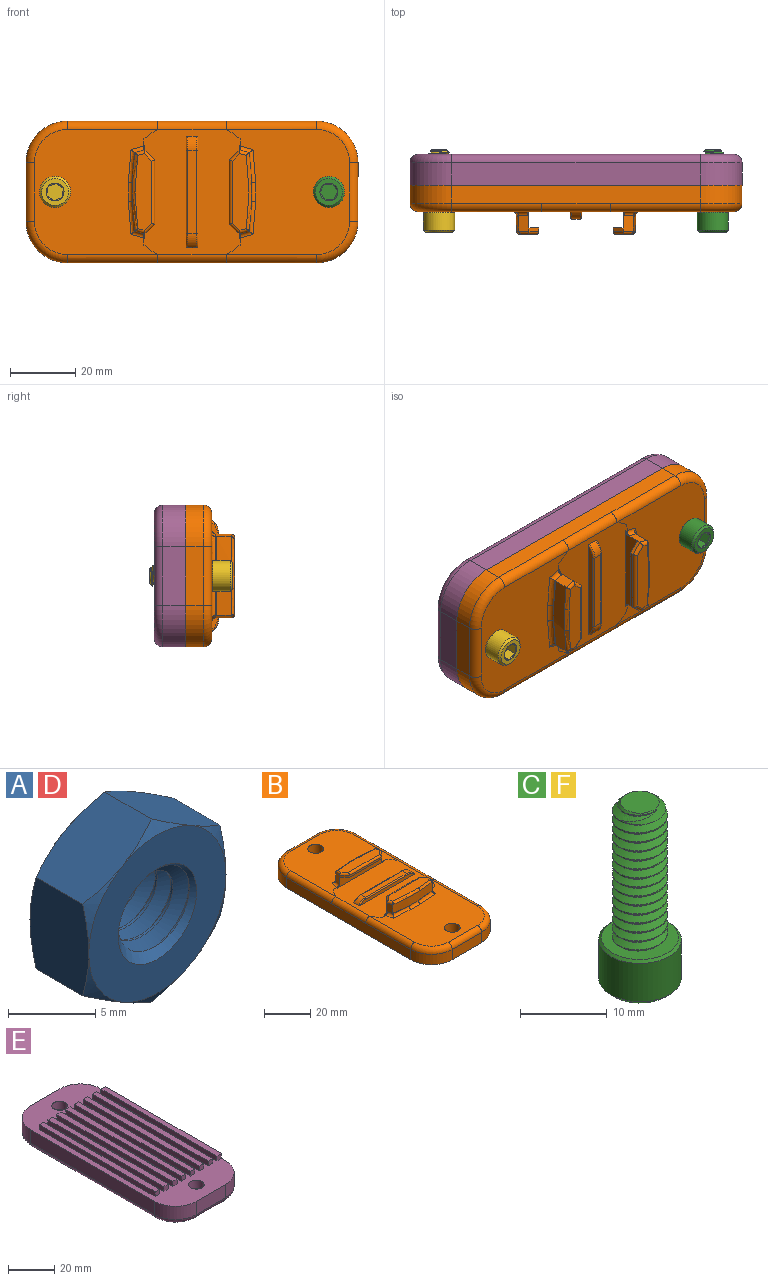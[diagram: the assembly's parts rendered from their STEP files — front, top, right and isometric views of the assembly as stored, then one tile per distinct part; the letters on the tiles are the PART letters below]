
ASSEMBLY  parts=6 mates=13
PART A: 26 faces, bbox 13.4x6.2x13.4 mm
  f0: bspline ~6.35x6.35mm, area 51.9mm2, adj f1,f11,f12,f19
  f1: cylinder r=2.35mm len=4.7mm, axis (0,-1,0), area 5.7mm2, adj f0,f2,f12,f19
  f2: bspline ~6.35x6.35mm, area 51.8mm2, adj f1,f11,f12,f19
  f3: plane 11.11x11.11mm, normal (0,1,0), area 65.3mm2, adj f11,f12,f13,f14,f15,f16,f17,f18
  f4: plane 6.08x5.3mm, normal (-0.5,0,-0.87), area 28.4mm2, adj f5,f9,f13,f18,f23,f24
  f5: plane 6.95x5.3mm, normal (-1,0,0), area 28.4mm2, adj f4,f6,f17,f18,f24,f25
  f6: plane 6.08x5.3mm, normal (-0.5,0,0.87), area 28.4mm2, adj f5,f7,f16,f17,f20,f25
  f7: plane 6.08x5.3mm, normal (0.5,0,0.87), area 28.4mm2, adj f6,f8,f15,f16,f20,f21
  f8: plane 6.95x5.3mm, normal (1,0,0), area 28.4mm2, adj f7,f9,f14,f15,f21,f22
  f9: plane 6.08x5.3mm, normal (0.5,0,-0.87), area 28.4mm2, adj f4,f8,f13,f14,f22,f23
  f10: plane 11.11x11.11mm, normal (0,-1,0), area 65.3mm2, adj f11,f19,f20,f21,f22,f23,f24,f25
  f11: cylinder r=3.17mm len=6.35mm, axis (0,-1,0), area 11.9mm2, adj f0,f2,f3,f10
  f12: cone r=3.17mm half-angle=45deg, axis (0,1,0), area 10.5mm2, adj f0,f1,f2,f3
  f13: cone r=5.56mm half-angle=60deg, axis (0,-1,0), area 3mm2, adj f3,f4,f9
  f14: cone r=5.56mm half-angle=60deg, axis (0,-1,0), area 3mm2, adj f3,f8,f9
  f15: cone r=5.56mm half-angle=60deg, axis (0,-1,0), area 3mm2, adj f3,f7,f8
  f16: cone r=5.56mm half-angle=60deg, axis (0,-1,0), area 3mm2, adj f3,f6,f7
  f17: cone r=5.56mm half-angle=60deg, axis (0,-1,0), area 3mm2, adj f3,f5,f6
  f18: cone r=5.56mm half-angle=60deg, axis (0,-1,0), area 3mm2, adj f3,f4,f5
  f19: cone r=3.17mm half-angle=45deg, axis (0,-1,0), area 10.5mm2, adj f0,f1,f2,f10
  f20: cone r=5.56mm half-angle=60deg, axis (0,1,0), area 3mm2, adj f6,f7,f10
  f21: cone r=5.56mm half-angle=60deg, axis (0,1,0), area 3mm2, adj f7,f8,f10
  f22: cone r=5.56mm half-angle=60deg, axis (0,1,0), area 3mm2, adj f8,f9,f10
  f23: cone r=5.56mm half-angle=60deg, axis (0,1,0), area 3mm2, adj f4,f9,f10
  f24: cone r=5.56mm half-angle=60deg, axis (0,1,0), area 3mm2, adj f4,f5,f10
  f25: cone r=5.56mm half-angle=60deg, axis (0,1,0), area 3mm2, adj f5,f6,f10
PART B: 124 faces, bbox 45.6x103.9x15.2 mm
  f0: bspline ~18.94x3.73mm, area 1mm2, adj f32,f44,f118,f119
  f1: bspline ~21.05x3.89mm, area 1mm2, adj f33,f49,f111,f112
  f2: plane 2.71x2.54mm, normal (0,-1,0), area 6.9mm2, adj f25,f27,f94,f108
  f3: plane 2.71x2.54mm, normal (0,1,0), area 6.9mm2, adj f25,f27,f94,f108
  f4: plane 71.12x2.71mm, normal (0,0,-1), area 192.8mm2, adj f5,f6,f106,f109
  f5: plane 2.71x2.54mm, normal (0,-1,0), area 6.9mm2, adj f4,f27,f106,f109
  f6: plane 2.71x2.54mm, normal (0,1,0), area 6.9mm2, adj f4,f27,f106,f109
  f7: plane 71.12x2.71mm, normal (0,0,-1), area 192.8mm2, adj f8,f9,f104,f107
  f8: plane 2.71x2.54mm, normal (0,-1,0), area 6.9mm2, adj f7,f27,f104,f107
  f9: plane 2.71x2.54mm, normal (0,1,0), area 6.9mm2, adj f7,f27,f104,f107
  f10: plane 71.12x2.71mm, normal (0,0,-1), area 192.8mm2, adj f11,f12,f102,f105
  f11: plane 2.71x2.54mm, normal (0,-1,0), area 6.9mm2, adj f10,f27,f102,f105
  f12: plane 2.71x2.54mm, normal (0,1,0), area 6.9mm2, adj f10,f27,f102,f105
  f13: plane 71.12x2.71mm, normal (0,0,-1), area 192.8mm2, adj f14,f15,f100,f103
  f14: plane 2.71x2.54mm, normal (0,-1,0), area 6.9mm2, adj f13,f27,f100,f103
  f15: plane 2.71x2.54mm, normal (0,1,0), area 6.9mm2, adj f13,f27,f100,f103
  f16: plane 71.12x2.71mm, normal (0,0,-1), area 192.8mm2, adj f17,f18,f98,f101
  f17: plane 2.71x2.54mm, normal (0,-1,0), area 6.9mm2, adj f16,f27,f98,f101
  f18: plane 2.71x2.54mm, normal (0,1,0), area 6.9mm2, adj f16,f27,f98,f101
  f19: plane 71.12x2.71mm, normal (0,0,-1), area 192.8mm2, adj f20,f21,f96,f99
  f20: plane 2.71x2.54mm, normal (0,-1,0), area 6.9mm2, adj f19,f27,f96,f99
  f21: plane 2.71x2.54mm, normal (0,1,0), area 6.9mm2, adj f19,f27,f96,f99
  f22: plane 71.12x2.71mm, normal (0,0,-1), area 192.8mm2, adj f23,f24,f95,f97
  f23: plane 2.71x2.54mm, normal (0,-1,0), area 6.9mm2, adj f22,f27,f95,f97
  f24: plane 2.71x2.54mm, normal (0,1,0), area 6.9mm2, adj f22,f27,f95,f97
  f25: plane 76.2x5.46mm, normal (1,0,0), area 235.5mm2, adj f2,f3,f27,f79,f80,f82,f83,f85
  f26: plane 17.98x5.46mm, normal (0,-1,0), area 98.2mm2, adj f27,f80,f81,f86
  f27: plane 101.6x43.38mm, normal (0,0,-1), area 2654.9mm2, adj f2,f3,f5,f6,f8,f9,f11,f12
  f28: plane 38.42x37.89mm, normal (0,0,1), area 1093.7mm2, adj f40,f77,f85,f87,f89,f91,f93,f118
  f29: plane 38.42x37.89mm, normal (0,0,1), area 1093.7mm2, adj f40,f76,f82,f84,f86,f88,f90,f111
  f30: plane 17.98x5.46mm, normal (0,1,0), area 98.2mm2, adj f27,f78,f79,f89
  f31: plane 4.73x3.1mm, normal (-0.97,0.26,0), area 15.2mm2, adj f36,f44,f45,f54,f66,f122,f123
  f32: plane 4.73x3.1mm, normal (0.97,0.26,0), area 15.2mm2, adj f0,f44,f47,f54,f63,f117,f118
  f33: plane 4.73x3.1mm, normal (-0.97,-0.26,0), area 15.2mm2, adj f1,f38,f49,f51,f55,f110,f111
  f34: plane 4.73x3.1mm, normal (0.97,-0.26,0), area 15.2mm2, adj f35,f39,f49,f51,f59,f115,f116
  f35: bspline ~18.94x3.73mm, area 1mm2, adj f34,f49,f114,f116
  f36: bspline ~21.05x3.89mm, area 1mm2, adj f31,f44,f121,f123
  f37: plane 19.82x1mm, normal (0,1,0), area 19.8mm2, adj f38,f39,f52,f58
  f38: plane 3x3mm, normal (-0.71,0.71,0), area 4.2mm2, adj f33,f37,f52,f56
  f39: plane 3x2.83mm, normal (0.73,0.69,0), area 4.1mm2, adj f34,f37,f52,f60
  f40: plane 38.57x30.25mm, normal (0,0,1), area 964.3mm2, adj f28,f29,f41,f42,f51,f54,f67,f68
  f41: plane 32.77x1.75mm, normal (0,-1,0), area 53.6mm2, adj f40,f72,f73,f74
  f42: plane 32.77x1.75mm, normal (0,1,0), area 53.6mm2, adj f40,f69,f70,f71
  f43: plane 25.65x2.65mm, normal (0,0,1), area 68mm2, adj f67,f68,f70,f73
  f44: cylinder r=95.04mm len=23.99mm, axis (0,0,-1), area 111.6mm2, adj f0,f31,f32,f36,f65,f120
  f45: plane 3x3mm, normal (-0.71,-0.71,0), area 4.2mm2, adj f31,f46,f53,f64
  f46: plane 19.82x1mm, normal (0,-1,0), area 19.8mm2, adj f45,f47,f53,f62
  f47: plane 3x2.83mm, normal (0.73,-0.69,0), area 4.1mm2, adj f32,f46,f53,f61
  f48: plane 23.42x4.86mm, normal (0,0,1), area 102.1mm2, adj f61,f62,f63,f64,f65,f66
  f49: cylinder r=95.04mm len=23.99mm, axis (0,0,-1), area 111.6mm2, adj f1,f33,f34,f35,f57,f113
  f50: plane 23.42x4.86mm, normal (0,0,1), area 102.1mm2, adj f55,f56,f57,f58,f59,f60
  f51: plane 28.42x5.14mm, normal (0,1,0), area 129mm2, adj f33,f34,f40,f52,f110,f115
  f52: plane 25.65x3mm, normal (0,0,-1), area 68.2mm2, adj f37,f38,f39,f51
  f53: plane 25.65x3mm, normal (0,0,-1), area 68.2mm2, adj f45,f46,f47,f54
  f54: plane 28.42x5.14mm, normal (0,-1,0), area 129mm2, adj f31,f32,f40,f53,f117,f122
  f55: cylinder r=1mm len=3.36mm, axis (-0.26,0.97,0), area 4.1mm2, adj f33,f50,f56,f57
  f56: cylinder r=1mm len=3.71mm, axis (0.71,0.71,0), area 5.9mm2, adj f38,f50,f55,f58
  f57: torus R=94.04mm, axis (0,0,1), area 36.6mm2, adj f49,f50,f55,f59
  f58: cylinder r=1mm len=19.82mm, axis (1,0,0), area 30.5mm2, adj f37,f50,f56,f60
  f59: cylinder r=1mm len=3.36mm, axis (-0.26,-0.97,0), area 4.1mm2, adj f34,f50,f57,f60
  f60: cylinder r=1mm len=3.69mm, axis (0.69,-0.73,0), area 5.7mm2, adj f39,f50,f58,f59
  f61: cylinder r=1mm len=3.69mm, axis (-0.69,-0.73,0), area 5.7mm2, adj f47,f48,f62,f63
  f62: cylinder r=1mm len=19.82mm, axis (-1,0,0), area 30.5mm2, adj f46,f48,f61,f64
  f63: cylinder r=1mm len=3.36mm, axis (0.26,-0.97,0), area 4.1mm2, adj f32,f48,f61,f65
  f64: cylinder r=1mm len=3.71mm, axis (-0.71,0.71,0), area 5.9mm2, adj f45,f48,f62,f66
  f65: torus R=94.04mm, axis (0,0,1), area 36.6mm2, adj f44,f48,f63,f66
  f66: cylinder r=1mm len=3.36mm, axis (0.26,0.97,0), area 4.1mm2, adj f31,f48,f64,f65
  f67: cylinder r=5mm len=4.18mm, axis (0,-1,0), area 13.1mm2, adj f40,f43,f69,f72
  f68: cylinder r=5mm len=4.18mm, axis (0,-1,0), area 13.1mm2, adj f40,f43,f71,f74
  f69: torus R=4.5mm, axis (0,1,0), area 3.6mm2, adj f40,f42,f67,f70
  f70: cylinder r=0.5mm len=25.65mm, axis (1,0,0), area 20.1mm2, adj f42,f43,f69,f71
  f71: torus R=4.5mm, axis (0,1,0), area 3.6mm2, adj f40,f42,f68,f70
  f72: torus R=4.5mm, axis (0,1,0), area 3.6mm2, adj f40,f41,f67,f73
  f73: cylinder r=0.5mm len=25.65mm, axis (-1,0,0), area 20.1mm2, adj f41,f43,f72,f74
  f74: torus R=4.5mm, axis (0,1,0), area 3.6mm2, adj f40,f41,f68,f73
  f75: plane 76.2x5.46mm, normal (-1,0,0), area 416.1mm2, adj f27,f78,f81,f90,f92,f93
  f76: cylinder r=3.38mm len=8mm, axis (0,0,-1), area 169.8mm2, adj f27,f29
  f77: cylinder r=3.38mm len=8mm, axis (0,0,-1), area 169.8mm2, adj f27,f28
  f78: cylinder r=12.7mm len=12.7mm, axis (0,0,1), area 108.9mm2, adj f27,f30,f75,f91
  f79: cylinder r=12.7mm len=12.7mm, axis (0,0,-1), area 108.9mm2, adj f25,f27,f30,f87
  f80: cylinder r=12.7mm len=12.7mm, axis (0,0,-1), area 108.9mm2, adj f25,f26,f27,f84
  f81: cylinder r=12.7mm len=12.7mm, axis (0,0,1), area 108.9mm2, adj f26,f27,f75,f88
  f82: cylinder r=2.54mm len=27.67mm, axis (0,-1,0), area 110.4mm2, adj f25,f29,f83,f84
  f83: cylinder r=2.54mm len=20.85mm, axis (0,1,0), area 83.2mm2, adj f25,f40,f82,f85
  f84: torus R=10.16mm, axis (0,0,-1), area 73.8mm2, adj f29,f80,f82,f86
  f85: cylinder r=2.54mm len=27.67mm, axis (0,-1,0), area 110.4mm2, adj f25,f28,f83,f87
  f86: cylinder r=2.54mm len=17.98mm, axis (1,0,0), area 71.7mm2, adj f26,f29,f84,f88
  f87: torus R=10.16mm, axis (0,0,-1), area 73.8mm2, adj f28,f79,f85,f89
  f88: torus R=10.16mm, axis (0,0,-1), area 73.8mm2, adj f29,f81,f86,f90
  f89: cylinder r=2.54mm len=17.98mm, axis (-1,0,0), area 71.7mm2, adj f28,f30,f87,f91
  f90: cylinder r=2.54mm len=27.67mm, axis (0,1,0), area 110.4mm2, adj f29,f75,f88,f92
  f91: torus R=10.16mm, axis (0,0,-1), area 73.8mm2, adj f28,f78,f89,f93
  f92: cylinder r=2.54mm len=20.85mm, axis (0,-1,0), area 83.2mm2, adj f40,f75,f90,f93
  f93: cylinder r=2.54mm len=27.67mm, axis (0,1,0), area 110.4mm2, adj f28,f75,f91,f92
  f94: plane 71.12x2.71mm, normal (0,0,-1), area 192.8mm2, adj f2,f3,f25,f108
  f95: plane 71.12x2.54mm, normal (1,0,0), area 180.6mm2, adj f22,f23,f24,f27
  f96: plane 71.12x2.54mm, normal (1,0,0), area 180.6mm2, adj f19,f20,f21,f27
  f97: plane 71.12x2.54mm, normal (-1,0,0), area 180.6mm2, adj f22,f23,f24,f27
  f98: plane 71.12x2.54mm, normal (1,0,0), area 180.6mm2, adj f16,f17,f18,f27
  f99: plane 71.12x2.54mm, normal (-1,0,0), area 180.6mm2, adj f19,f20,f21,f27
  f100: plane 71.12x2.54mm, normal (1,0,0), area 180.6mm2, adj f13,f14,f15,f27
  f101: plane 71.12x2.54mm, normal (-1,0,0), area 180.6mm2, adj f16,f17,f18,f27
  f102: plane 71.12x2.54mm, normal (1,0,0), area 180.6mm2, adj f10,f11,f12,f27
  f103: plane 71.12x2.54mm, normal (-1,0,0), area 180.6mm2, adj f13,f14,f15,f27
  f104: plane 71.12x2.54mm, normal (1,0,0), area 180.6mm2, adj f7,f8,f9,f27
  f105: plane 71.12x2.54mm, normal (-1,0,0), area 180.6mm2, adj f10,f11,f12,f27
  f106: plane 71.12x2.54mm, normal (1,0,0), area 180.6mm2, adj f4,f5,f6,f27
  f107: plane 71.12x2.54mm, normal (-1,0,0), area 180.6mm2, adj f7,f8,f9,f27
  f108: plane 71.12x2.54mm, normal (1,0,0), area 180.6mm2, adj f2,f3,f27,f94
  f109: plane 71.12x2.54mm, normal (-1,0,0), area 180.6mm2, adj f4,f5,f6,f27
  f110: cylinder r=1.27mm len=1.4mm, axis (0.26,-0.97,0), area 1mm2, adj f33,f40,f51,f111
  f111: cylinder r=1.27mm len=3.94mm, axis (0.26,-0.97,0), area 6.4mm2, adj f1,f29,f33,f110,f112
  f112: bspline ~16.98x2.74mm, area 19.2mm2, adj f1,f29,f111,f113
  f113: torus R=96.31mm, axis (0,0,-1), area 11.2mm2, adj f29,f49,f112,f114
  f114: bspline ~13.49x2.2mm, area 19.2mm2, adj f29,f35,f113,f116
  f115: cylinder r=1.27mm len=1.4mm, axis (0.26,0.97,0), area 1mm2, adj f34,f40,f51,f116
  f116: cylinder r=1.27mm len=3.94mm, axis (0.26,0.97,0), area 6.4mm2, adj f29,f34,f35,f114,f115
  f117: cylinder r=1.27mm len=1.4mm, axis (-0.26,0.97,0), area 1mm2, adj f32,f40,f54,f118
  f118: cylinder r=1.27mm len=3.94mm, axis (-0.26,0.97,0), area 6.4mm2, adj f0,f28,f32,f117,f119
  f119: bspline ~13.43x2.19mm, area 19.2mm2, adj f0,f28,f118,f120
  f120: torus R=96.31mm, axis (0,0,-1), area 11.2mm2, adj f28,f44,f119,f121
  f121: bspline ~17.29x2.76mm, area 19.2mm2, adj f28,f36,f120,f123
  f122: cylinder r=1.27mm len=1.4mm, axis (-0.26,-0.97,0), area 1mm2, adj f31,f40,f54,f123
  f123: cylinder r=1.27mm len=3.94mm, axis (-0.26,-0.97,0), area 6.4mm2, adj f28,f31,f36,f121,f122
PART C: 24 faces, bbox 10.6x10.6x26.9 mm
  f0: cylinder r=3.17mm len=18.1mm, axis (0,0,1), area 49.6mm2, adj f2,f4,f5,f6
  f1: plane 4.45x4.45mm, normal (0,0,1), area 15.5mm2, adj f2
  f2: cone r=2.22mm half-angle=45deg, axis (0,0,-1), area 12.3mm2, adj f0,f1,f3,f4,f5
  f3: cylinder r=2.35mm len=18.92mm, axis (0,0,-1), area 40mm2, adj f2,f4,f5,f6
  f4: bspline ~19.74x7.33mm, area 241.5mm2, adj f0,f2,f3,f6
  f5: bspline ~20.16x7.33mm, area 240.1mm2, adj f0,f2,f3,f6
  f6: plane 9.39x9.39mm, normal (0,0,1), area 37.8mm2, adj f0,f3,f4,f5,f23
  f7: cylinder r=4.76mm len=9.53mm, axis (0,0,1), area 161.5mm2, adj f22,f23
  f8: plane 8.26x8.26mm, normal (0,0,-1), area 29.8mm2, adj f9,f10,f11,f12,f13,f14,f22
  f9: cone r=2.75mm half-angle=45deg, axis (0,0,-1), area 0mm2, adj f8,f16
  f10: cone r=2.75mm half-angle=45deg, axis (0,0,-1), area 0mm2, adj f8,f17
  f11: cone r=2.75mm half-angle=45deg, axis (0,0,-1), area 0mm2, adj f8,f18
  f12: cone r=2.75mm half-angle=45deg, axis (0,0,-1), area 0mm2, adj f8,f19
  f13: cone r=2.75mm half-angle=45deg, axis (0,0,-1), area 0mm2, adj f8,f20
  f14: cone r=2.75mm half-angle=45deg, axis (0,0,-1), area 0mm2, adj f8,f21
  f15: plane 5.5x4.76mm, normal (0,0,-1), area 19.6mm2, adj f16,f17,f18,f19,f20,f21
  f16: plane 4.61x3.42mm, normal (-0.5,-0.87,0), area 9.2mm2, adj f9,f15,f17,f21
  f17: plane 4.62x3.8mm, normal (-1,0,0), area 9.2mm2, adj f10,f15,f16,f18
  f18: plane 4.61x3.42mm, normal (-0.5,0.87,0), area 9.2mm2, adj f11,f15,f17,f19
  f19: plane 4.61x3.42mm, normal (0.5,0.87,0), area 9.2mm2, adj f12,f15,f18,f20
  f20: plane 4.62x3.8mm, normal (1,0,0), area 9.2mm2, adj f13,f15,f19,f21
  f21: plane 4.61x3.42mm, normal (0.5,-0.87,0), area 9.2mm2, adj f14,f15,f16,f20
  f22: cone r=4.13mm half-angle=45deg, axis (0,0,1), area 25.1mm2, adj f7,f8
  f23: cone r=4.76mm half-angle=45deg, axis (0,0,-1), area 13mm2, adj f6,f7
PART D: same geometry as A
PART E: 74 faces, bbox 45.5x103.7x12.1 mm
  f0: plane 96.52x38.3mm, normal (0,0,-1), area 3354.9mm2, adj f6,f7,f8,f9,f10,f11,f13,f14
  f1: plane 76.2x6.99mm, normal (-1,0,0), area 532.3mm2, adj f5,f22,f25,f33
  f2: plane 17.98x6.99mm, normal (0,1,0), area 125.6mm2, adj f5,f22,f23,f29
  f3: plane 76.21x7mm, normal (1,0,0), area 532.3mm2, adj f5,f23,f24,f26,f72
  f4: plane 17.98x6.99mm, normal (0,-1,0), area 125.6mm2, adj f5,f24,f25,f30
  f5: plane 101.6x43.39mm, normal (0,0,1), area 2655.3mm2, adj f1,f2,f3,f4,f20,f21,f22,f23
  f6: plane 6.99x5.08mm, normal (0,1,0), area 35.5mm2, adj f0,f7,f11,f12
  f7: plane 6.05x5.08mm, normal (0.87,0.5,0), area 35.5mm2, adj f0,f6,f8,f12
  f8: plane 6.05x5.08mm, normal (0.87,-0.5,0), area 35.5mm2, adj f0,f7,f9,f12
  f9: plane 6.99x5.08mm, normal (0,-1,0), area 35.5mm2, adj f0,f8,f10,f12
  f10: plane 6.05x5.08mm, normal (-0.87,-0.5,0), area 35.5mm2, adj f0,f9,f11,f12
  f11: plane 6.05x5.08mm, normal (-0.87,0.5,0), area 35.5mm2, adj f0,f6,f10,f12
  f12: plane 13.97x12.1mm, normal (0,0,-1), area 90.9mm2, adj f6,f7,f8,f9,f10,f11,f20
  f13: plane 6.05x5.08mm, normal (0.87,0.5,0), area 35.5mm2, adj f0,f14,f18,f19
  f14: plane 6.05x5.08mm, normal (0.87,-0.5,0), area 35.5mm2, adj f0,f13,f15,f19
  f15: plane 6.99x5.08mm, normal (0,-1,0), area 35.5mm2, adj f0,f14,f16,f19
  f16: plane 6.05x5.08mm, normal (-0.87,-0.5,0), area 35.5mm2, adj f0,f15,f17,f19
  f17: plane 6.05x5.08mm, normal (-0.87,0.5,0), area 35.5mm2, adj f0,f16,f18,f19
  f18: plane 6.99x5.08mm, normal (0,1,0), area 35.5mm2, adj f0,f13,f17,f19
  f19: plane 13.97x12.1mm, normal (0,0,-1), area 90.9mm2, adj f13,f14,f15,f16,f17,f18,f21
  f20: cylinder r=3.38mm len=6.76mm, axis (0,0,-1), area 94.3mm2, adj f5,f12
  f21: cylinder r=3.38mm len=6.76mm, axis (0,0,-1), area 94.3mm2, adj f5,f19
  f22: cylinder r=12.7mm len=12.7mm, axis (0,0,-1), area 139.3mm2, adj f1,f2,f5,f31
  f23: cylinder r=12.7mm len=12.7mm, axis (0,0,1), area 139.3mm2, adj f2,f3,f5,f27
  f24: cylinder r=12.7mm len=12.7mm, axis (0,0,-1), area 139.3mm2, adj f3,f4,f5,f28
  f25: cylinder r=12.7mm len=12.7mm, axis (0,0,1), area 139.3mm2, adj f1,f4,f5,f32
  f26: cylinder r=2.54mm len=76.2mm, axis (0,1,0), area 304mm2, adj f0,f3,f27,f28
  f27: torus R=10.16mm, axis (0,0,-1), area 73.8mm2, adj f0,f23,f26,f29
  f28: torus R=10.16mm, axis (0,0,-1), area 73.8mm2, adj f0,f24,f26,f30
  f29: cylinder r=2.54mm len=17.98mm, axis (-1,0,0), area 71.7mm2, adj f0,f2,f27,f31
  f30: cylinder r=2.54mm len=17.98mm, axis (1,0,0), area 71.7mm2, adj f0,f4,f28,f32
  f31: torus R=10.16mm, axis (0,0,-1), area 73.8mm2, adj f0,f22,f29,f33
  f32: torus R=10.16mm, axis (0,0,-1), area 73.8mm2, adj f0,f25,f30,f33
  f33: cylinder r=2.54mm len=76.2mm, axis (0,-1,0), area 304mm2, adj f0,f1,f31,f32
  f34: plane 2.71x2.54mm, normal (0,1,0), area 6.9mm2, adj f5,f35,f37,f38
  f35: plane 71.12x2.54mm, normal (-1,0,0), area 180.6mm2, adj f5,f34,f36,f38
  f36: plane 2.71x2.54mm, normal (0,-1,0), area 6.9mm2, adj f5,f35,f37,f38
  f37: plane 71.12x2.54mm, normal (1,0,0), area 180.6mm2, adj f5,f34,f36,f38
  f38: plane 71.12x2.71mm, normal (0,0,1), area 192.8mm2, adj f34,f35,f36,f37
  f39: plane 71.12x2.54mm, normal (1,0,0), area 180.6mm2, adj f5,f40,f42,f43
  f40: plane 2.71x2.54mm, normal (0,1,0), area 6.9mm2, adj f5,f39,f41,f43
  f41: plane 71.12x2.54mm, normal (-1,0,0), area 180.6mm2, adj f5,f40,f42,f43
  f42: plane 2.71x2.54mm, normal (0,-1,0), area 6.9mm2, adj f5,f39,f41,f43
  f43: plane 71.12x2.71mm, normal (0,0,1), area 192.8mm2, adj f39,f40,f41,f42
  f44: plane 71.12x2.54mm, normal (1,0,0), area 180.6mm2, adj f5,f45,f47,f48
  f45: plane 2.71x2.54mm, normal (0,1,0), area 6.9mm2, adj f5,f44,f46,f48
  f46: plane 71.12x2.54mm, normal (-1,0,0), area 180.6mm2, adj f5,f45,f47,f48
  f47: plane 2.71x2.54mm, normal (0,-1,0), area 6.9mm2, adj f5,f44,f46,f48
  f48: plane 71.12x2.71mm, normal (0,0,1), area 192.8mm2, adj f44,f45,f46,f47
  f49: plane 71.12x2.54mm, normal (1,0,0), area 180.6mm2, adj f5,f50,f52,f53
  f50: plane 2.71x2.54mm, normal (0,1,0), area 6.9mm2, adj f5,f49,f51,f53
  f51: plane 71.12x2.54mm, normal (-1,0,0), area 180.6mm2, adj f5,f50,f52,f53
  f52: plane 2.71x2.54mm, normal (0,-1,0), area 6.9mm2, adj f5,f49,f51,f53
  f53: plane 71.12x2.71mm, normal (0,0,1), area 192.8mm2, adj f49,f50,f51,f52
  f54: plane 71.12x2.54mm, normal (1,0,0), area 180.6mm2, adj f5,f55,f57,f58
  f55: plane 2.71x2.54mm, normal (0,1,0), area 6.9mm2, adj f5,f54,f56,f58
  f56: plane 71.12x2.54mm, normal (-1,0,0), area 180.6mm2, adj f5,f55,f57,f58
  f57: plane 2.71x2.54mm, normal (0,-1,0), area 6.9mm2, adj f5,f54,f56,f58
  f58: plane 71.12x2.71mm, normal (0,0,1), area 192.8mm2, adj f54,f55,f56,f57
  f59: plane 71.12x2.54mm, normal (1,0,0), area 180.6mm2, adj f5,f60,f62,f63
  f60: plane 2.71x2.54mm, normal (0,1,0), area 6.9mm2, adj f5,f59,f61,f63
  f61: plane 71.12x2.54mm, normal (-1,0,0), area 180.6mm2, adj f5,f60,f62,f63
  f62: plane 2.71x2.54mm, normal (0,-1,0), area 6.9mm2, adj f5,f59,f61,f63
  f63: plane 71.12x2.71mm, normal (0,0,1), area 192.8mm2, adj f59,f60,f61,f62
  f64: plane 71.12x2.54mm, normal (1,0,0), area 180.6mm2, adj f5,f65,f67,f68
  f65: plane 2.71x2.54mm, normal (0,1,0), area 6.9mm2, adj f5,f64,f66,f68
  f66: plane 71.12x2.54mm, normal (-1,0,0), area 180.6mm2, adj f5,f65,f67,f68
  f67: plane 2.71x2.54mm, normal (0,-1,0), area 6.9mm2, adj f5,f64,f66,f68
  f68: plane 71.12x2.71mm, normal (0,0,1), area 192.8mm2, adj f64,f65,f66,f67
  f69: plane 2.71x2.54mm, normal (0,1,0), area 6.9mm2, adj f5,f70,f72,f73
  f70: plane 71.12x2.54mm, normal (-1,0,0), area 180.6mm2, adj f5,f69,f71,f73
  f71: plane 2.71x2.54mm, normal (0,-1,0), area 6.9mm2, adj f5,f70,f72,f73
  f72: plane 71.13x2.55mm, normal (1,0,0), area 180.6mm2, adj f3,f69,f71,f73
  f73: plane 71.12x2.71mm, normal (0,0,1), area 192.8mm2, adj f69,f70,f71,f72
PART F: same geometry as C
PLACE A rot(axis=(-0.5,0,0.87),180deg) t=(-24.47,-3.3,64.23)mm
PLACE B rot(axis=(0.58,0.58,-0.58),120deg) t=(17.44,-10.12,64.23)mm fixed
PLACE C rot(axis=(-0.16,-0.7,-0.7),161.9deg) t=(59.35,0.93,64.23)mm
PLACE D t=(59.35,-3.3,64.23)mm
PLACE E rot(axis=(0.58,0.58,-0.58),120deg) t=(17.44,-10.12,64.23)mm
PLACE F rot(axis=(-0.32,0.67,0.67),144.7deg) t=(-24.47,0.93,64.23)mm
MATE planar E.f21 <-> A.f11  axis (0,1,0) through (-24.47,-5.68,64.23)mm
MATE planar C.f0 <-> B.f78  axis (0,1,0) through (59.35,-18.12,64.23)mm
MATE parallel E.f17 <-> A.f8  axis (0.5,0,0.87) through (-27.5,-3.14,58.99)mm
MATE cylindrical F.f0 <-> B.f76  axis (0,1,0) through (-24.47,0.93,64.23)mm
MATE planar B.f29 <-> F.f6  axis (0,-1,0) through (-14.56,-18.12,64.23)mm
MATE cylindrical B.f77 <-> E.f20  axis (0,1,0) through (59.35,-14.12,64.23)mm
MATE cylindrical C.f0 <-> B.f77  axis (0,-1,0) through (59.35,-18.44,64.23)mm
MATE planar E.f12 <-> D.f11  axis (0,1,0) through (65.39,-5.68,64.23)mm
MATE parallel E.f11 <-> D.f4  axis (0.5,0,0.87) through (56.32,-3.14,58.99)mm
MATE cylindrical A.f11 <-> F.f0  axis (0,1,0) through (-24.47,-0.91,64.23)mm
MATE cylindrical E.f21 <-> B.f76  axis (0,-1,0) through (-24.47,-10.12,64.23)mm
MATE cylindrical C.f0 <-> D.f11  axis (0,1,0) through (59.35,0.93,64.23)mm
MATE planar B.f27 <-> E.f5  axis (0,1,0) through (17.44,-10.12,65.02)mm
